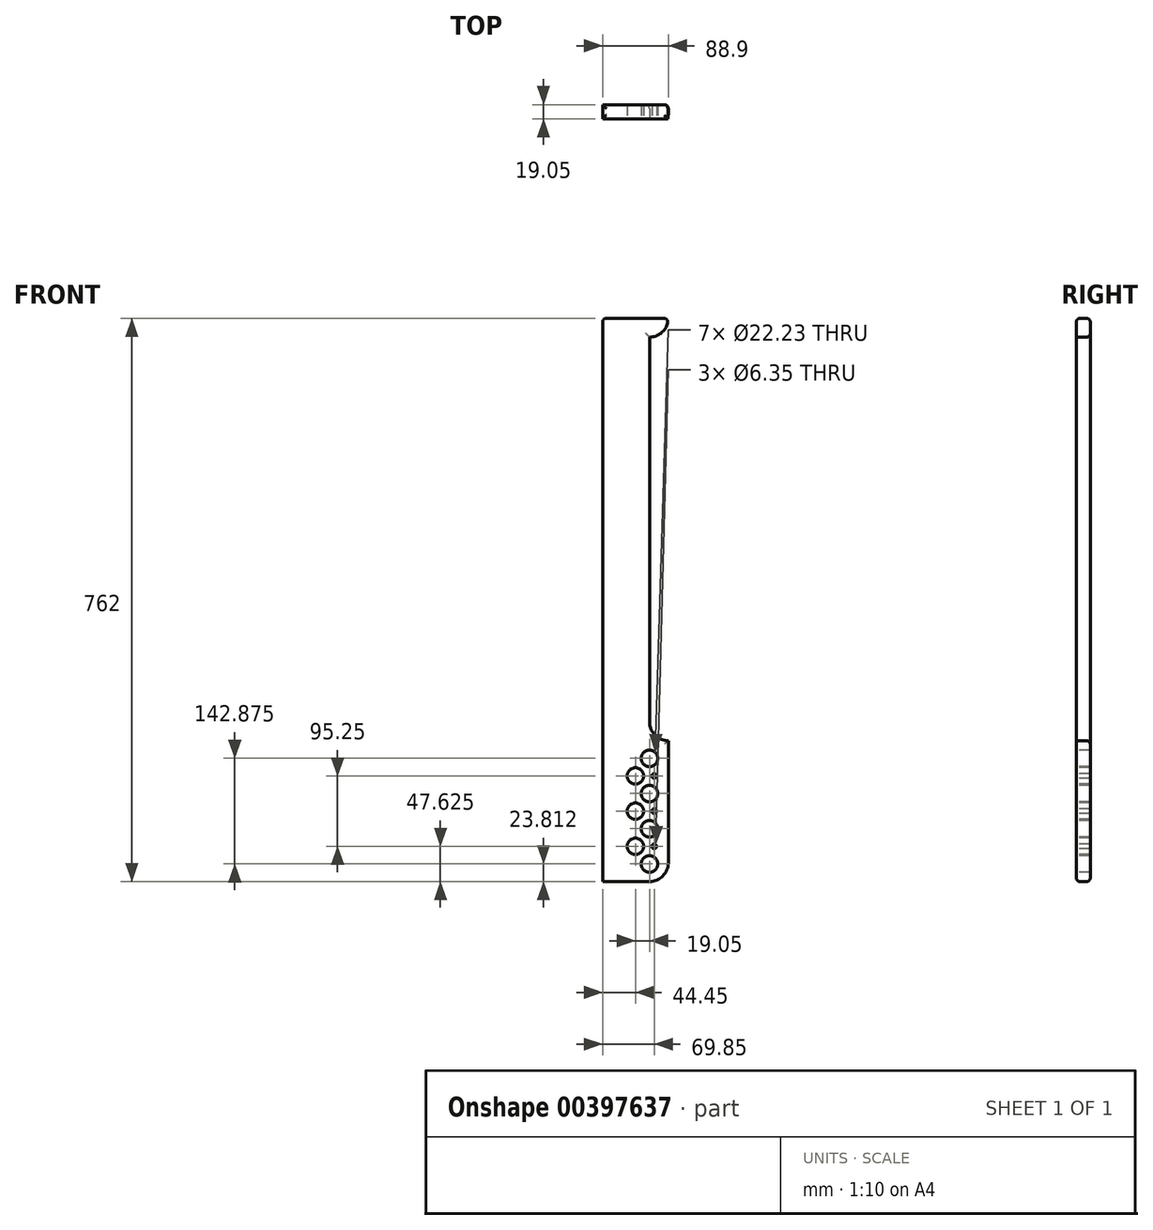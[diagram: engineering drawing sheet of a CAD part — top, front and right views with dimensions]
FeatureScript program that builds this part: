
annotation { "Feature Type Name" : "Feature", "Feature Type Description" : "" }
export const myFeature = defineFeature(function(context is Context, id is Id, definition is map)
    precondition{}
    {
        {
            var Q0;
            Q0=qCreatedBy(makeId("Top.planeOp"),FACE);
            var sketch = newSketch(context, id + "F0", { "sketchPlane" : qUnion([Q0])});
            skLineSegment(sketch, "E0.bottom", {"start": v(0, 0) * mm, "end": v(-88.9, 0) * mm});
            skLineSegment(sketch, "E0.top", {"start": v(0, -19.05) * mm, "end": v(-88.9, -19.05) * mm});
            skLineSegment(sketch, "E0.left", {"start": v(0, 0) * mm, "end": v(0, -19.05) * mm});
            skLineSegment(sketch, "E0.right", {"start": v(-88.9, 0) * mm, "end": v(-88.9, -19.05) * mm});
            skSolve(sketch);
        }
        {
            var Q0;
            Q0 = qSketchRegion(id + "F0", true);
            extrude(context, id + "F1", {"entities" : qUnion([Q0]), "depth" : 762 * mm});
        }
        {
            var Q0;
            Q0=makeQuery(id+"F1.opExtrude","SWEPT_FACE",FACE,{"disambiguationData":[OSD([sQuery(id+"F0.wireOp",EDGE,"E0.right")])]});
            cPlane(context, id + "F2", {"entities" : qUnion([Q0]), "cplaneType" : CPlaneType.OFFSET, "offset" : 44.45 * mm, "oppositeDirection" : true, "width" : 152.4 * mm, "height" : 152.4 * mm});
        }
        {
            var Q0;
            Q0=makeQuery(id+"F1.opExtrude","SWEPT_FACE",FACE,{"disambiguationData":[OSD([sQuery(id+"F0.wireOp",EDGE,"E0.top")])]});
            var sketch = newSketch(context, id + "F3", { "sketchPlane" : qUnion([Q0])});
            skLineSegment(sketch, "E1", {"start": v(0, 762) * mm, "end": v(-25.4, 762) * mm, "construction": true});
            skLineSegment(sketch, "E2", {"start": v(0, 762) * mm, "end": v(0, 762) * mm});
            skLineSegment(sketch, "E3", {"start": v(-25.4, 736.6) * mm, "end": v(-25.4, 736.6) * mm});
            skLineSegment(sketch, "E4", {"start": v(0, 0) * mm, "end": v(0, 190.5) * mm, "construction": true});
            skLineSegment(sketch, "E5", {"start": v(0, 190.5) * mm, "end": v(0, 190.5) * mm});
            skLineSegment(sketch, "E6", {"start": v(-25.4, 215.9) * mm, "end": v(-25.4, 215.9) * mm});
            skLineSegment(sketch, "E7", {"start": v(-25.4, 215.9) * mm, "end": v(-25.4, 736.6) * mm});
            skLineSegment(sketch, "E8", {"start": v(0, 762) * mm, "end": v(104.75, 762) * mm});
            skLineSegment(sketch, "E9", {"start": v(104.75, 762) * mm, "end": v(104.75, 190.5) * mm});
            skLineSegment(sketch, "E10", {"start": v(104.75, 190.5) * mm, "end": v(0, 190.5) * mm});
            skPoint(sketch, "E11.visualSharp", {"position": v(0, 736.6) * mm});
            skArc(sketch, "E11.filletArc", {"start": v(-25.4, 736.6) * mm, "mid": v(-7.44, 744.04) * mm, "end": v(0, 762) * mm});
            skPoint(sketch, "E12.visualSharp", {"position": v(-25.4, 190.5) * mm});
            skArc(sketch, "E12.filletArc", {"start": v(-25.4, 215.9) * mm, "mid": v(-17.96, 197.94) * mm, "end": v(0, 190.5) * mm});
            skSolve(sketch);
        }
        {
            var Q0;
            Q0=makeQuery(id+"F1.opExtrude","SWEPT_FACE",FACE,{"disambiguationData":[OSD([sQuery(id+"F0.wireOp",EDGE,"E0.top")])]});
            var sketch = newSketch(context, id + "F4", { "sketchPlane" : qUnion([Q0])});
            skLineSegment(sketch, "E13", {"start": v(-25.4, 0) * mm, "end": v(-25.4, 0) * mm});
            skLineSegment(sketch, "E14", {"start": v(-25.4, 0) * mm, "end": v(-25.4, 25.4) * mm, "construction": true});
            skLineSegment(sketch, "E15", {"start": v(-25.4, 25.4) * mm, "end": v(0, 25.4) * mm, "construction": true});
            skLineSegment(sketch, "E16", {"start": v(0, 25.4) * mm, "end": v(0, 25.4) * mm});
            skPoint(sketch, "E17.visualSharp", {"position": v(0, 0) * mm});
            skArc(sketch, "E17.filletArc", {"start": v(-25.4, 0) * mm, "mid": v(-7.44, 7.44) * mm, "end": v(0, 25.4) * mm});
            skLineSegment(sketch, "E18", {"start": v(0, 25.4) * mm, "end": v(15.67, 25.4) * mm});
            skLineSegment(sketch, "E19", {"start": v(15.67, 25.4) * mm, "end": v(15.67, -5.8) * mm});
            skLineSegment(sketch, "E20", {"start": v(15.67, -5.8) * mm, "end": v(-25.1, -5.8) * mm});
            skLineSegment(sketch, "E21", {"start": v(-25.1, -5.8) * mm, "end": v(-25.4, 0) * mm});
            skSolve(sketch);
        }
        {
            var Q0;
            Q0 = qSketchRegion(id + "F3", true);
            var Q1;
            Q1 = qSketchRegion(id + "F4", true);
            extrude(context, id + "F5", {"entities" : qUnion([Q0, Q1]), "operationType" : NewBodyOperationType.REMOVE, "oppositeDirection" : true, "depth" : 25.4 * mm});
        }
        {
            var Q0;
            Q0=makeQuery(id+"F1.opExtrude","SWEPT_FACE",FACE,{"disambiguationData":[OSD([sQuery(id+"F0.wireOp",EDGE,"E0.top")])]});
            var sketch = newSketch(context, id + "F6", { "sketchPlane" : qUnion([Q0])});
            skLineSegment(sketch, "E22", {"start": v(0, 0) * mm, "end": v(-44.45, 0) * mm, "construction": true});
            skLineSegment(sketch, "E23", {"start": v(0, 190.5) * mm, "end": v(-44.45, 190.5) * mm, "construction": true});
            skLineSegment(sketch, "E24", {"start": v(-44.45, 190.5) * mm, "end": v(-44.45, 142.88) * mm, "construction": true});
            skLineSegment(sketch, "E25", {"start": v(-44.45, 142.88) * mm, "end": v(-44.45, 95.25) * mm, "construction": true});
            skLineSegment(sketch, "E26", {"start": v(-44.45, 95.25) * mm, "end": v(-44.45, 47.62) * mm, "construction": true});
            skLineSegment(sketch, "E27", {"start": v(-44.45, 47.62) * mm, "end": v(-44.45, 0) * mm, "construction": true});
            skCircle(sketch, "E28", {"center": v(-44.45, 142.88) * mm, "radius": 11.11 * mm});
            skLineSegment(sketch, "E29", {"start": v(-25.4, 142.88) * mm, "end": v(-25.4, 166.69) * mm, "construction": true});
            skCircle(sketch, "E30", {"center": v(-25.4, 166.69) * mm, "radius": 11.11 * mm});
            skLineSegment(sketch, "E31", {"start": v(-33.34, 142.88) * mm, "end": v(-19.05, 142.88) * mm});
            skCircle(sketch, "E32", {"center": v(-19.05, 142.88) * mm, "radius": 3.18 * mm});
            skCircle(sketch, "E33.0.1.0", {"center": v(-44.45, 95.25) * mm, "radius": 11.11 * mm});
            skCircle(sketch, "E33.0.2.0", {"center": v(-44.45, 47.62) * mm, "radius": 11.11 * mm});
            skLineSegment(sketch, "E33.direction1", {"start": v(-44.45, 142.88) * mm, "end": v(-19.05, 142.88) * mm, "construction": true});
            skCircle(sketch, "E34.0.1.0", {"center": v(-25.4, 119.06) * mm, "radius": 11.11 * mm});
            skCircle(sketch, "E34.0.2.0", {"center": v(-25.4, 71.44) * mm, "radius": 11.11 * mm});
            skCircle(sketch, "E34.0.3.0", {"center": v(-25.4, 23.81) * mm, "radius": 11.11 * mm});
            skLineSegment(sketch, "E34.direction1", {"start": v(-25.4, 166.69) * mm, "end": v(6.35, 166.69) * mm, "construction": true});
            skLineSegment(sketch, "E34.direction2", {"start": v(-25.4, 166.69) * mm, "end": v(-25.4, 119.06) * mm, "construction": true});
            skCircle(sketch, "E35.0.1.0", {"center": v(-19.05, 95.25) * mm, "radius": 3.18 * mm});
            skCircle(sketch, "E35.0.2.0", {"center": v(-19.05, 47.62) * mm, "radius": 3.18 * mm});
            skLineSegment(sketch, "E35.direction1", {"start": v(-19.05, 142.88) * mm, "end": v(11.11, 142.88) * mm, "construction": true});
            skLineSegment(sketch, "E35.direction2", {"start": v(-19.05, 142.88) * mm, "end": v(-19.05, 95.25) * mm, "construction": true});
            skLineSegment(sketch, "E36", {"start": v(-44.45, 142.88) * mm, "end": v(-19.05, 142.88) * mm});
            skSolve(sketch);
        }
        {
            var Q0;
            Q0 = qSketchRegion(id + "F6", true);
            extrude(context, id + "F7", {"entities" : qUnion([Q0]), "operationType" : NewBodyOperationType.REMOVE, "oppositeDirection" : true, "depth" : 25.4 * mm});
        }
        {
            var Q0;
            Q0=makeQuery(id+"FR74C55Pt3mRpPs_1.1.F5.boolean.opBoolean","COPY",EDGE,{"derivedFrom":makeQuery(id+"FR74C55Pt3mRpPs_1.1.F5.opExtrude","CAP_EDGE",EDGE,{"disambiguationData":[OSD([sQuery(id+"F3.wireOp",EDGE,"E7")])],"isStart":true})});
            var Q1;
            Q1=makeQuery(id+"FR74C55Pt3mRpPs_1.1.F5.boolean.opBoolean","INTERSECT",EDGE,{"derivedFrom":[makeQuery(id+"F1.opExtrude","SWEPT_FACE",FACE,{"disambiguationData":[OSD([sQuery(id+"F0.wireOp",EDGE,"E0.bottom")])]}),makeQuery(id+"FR74C55Pt3mRpPs_1.1.F5.opExtrude","SWEPT_FACE",FACE,{"disambiguationData":[OSD([sQuery(id+"F3.wireOp",EDGE,"E7")])]})]});
            var Q2;
            Q2=makeQuery(id+"F5.boolean.opBoolean","COPY",EDGE,{"derivedFrom":makeQuery(id+"F5.opExtrude","CAP_EDGE",EDGE,{"disambiguationData":[OSD([sQuery(id+"F3.wireOp",EDGE,"E7")])],"isStart":true})});
            var Q3;
            Q3=makeQuery(id+"F5.boolean.opBoolean","INTERSECT",EDGE,{"derivedFrom":[makeQuery(id+"F1.opExtrude","SWEPT_FACE",FACE,{"disambiguationData":[OSD([sQuery(id+"F0.wireOp",EDGE,"E0.bottom")])]}),makeQuery(id+"F5.opExtrude","SWEPT_FACE",FACE,{"disambiguationData":[OSD([sQuery(id+"F3.wireOp",EDGE,"E7")])]})]});
            var Q4;
            Q4=makeQuery(id+"F1.opExtrude","SWEPT_EDGE",EDGE,{"disambiguationData":[OSD([sQuery(id+"F0.wireOp",EDGE,"E0.top"),sQuery(id+"F0.wireOp",EDGE,"E0.left")])]});
            var Q5;
            Q5=makeQuery(id+"F1.opExtrude","SWEPT_EDGE",EDGE,{"disambiguationData":[OSD([sQuery(id+"F0.wireOp",EDGE,"E0.bottom"),sQuery(id+"F0.wireOp",EDGE,"E0.left")])]});
            var Q6;
            Q6=makeQuery(id+"FR74C55Pt3mRpPs_1.1.F5.boolean.opBoolean","COPY",EDGE,{"derivedFrom":makeQuery(id+"FR74C55Pt3mRpPs_1.1.F5.opExtrude","CAP_EDGE",EDGE,{"disambiguationData":[OSD([sQuery(id+"F3.wireOp",EDGE,"E11.filletArc")])],"isStart":true})});
            var Q7;
            Q7=makeQuery(id+"F1.opExtrude","CAP_EDGE",EDGE,{"disambiguationData":[OSD([sQuery(id+"F0.wireOp",EDGE,"E0.top")])],"isStart":false});
            var Q8;
            Q8=makeQuery(id+"F5.boolean.opBoolean","COPY",EDGE,{"derivedFrom":makeQuery(id+"F5.opExtrude","CAP_EDGE",EDGE,{"disambiguationData":[OSD([sQuery(id+"F3.wireOp",EDGE,"E11.filletArc")])],"isStart":true})});
            var Q9;
            Q9=makeQuery(id+"F5.boolean.opBoolean","INTERSECT",EDGE,{"derivedFrom":[makeQuery(id+"F1.opExtrude","SWEPT_FACE",FACE,{"disambiguationData":[OSD([sQuery(id+"F0.wireOp",EDGE,"E0.bottom")])]}),makeQuery(id+"F5.opExtrude","SWEPT_FACE",FACE,{"disambiguationData":[OSD([sQuery(id+"F3.wireOp",EDGE,"E11.filletArc")])]})]});
            var Q10;
            Q10=makeQuery(id+"F1.opExtrude","CAP_EDGE",EDGE,{"disambiguationData":[OSD([sQuery(id+"F0.wireOp",EDGE,"E0.bottom")])],"isStart":false});
            var Q11;
            Q11=makeQuery(id+"FR74C55Pt3mRpPs_1.1.F5.boolean.opBoolean","INTERSECT",EDGE,{"derivedFrom":[makeQuery(id+"F1.opExtrude","SWEPT_FACE",FACE,{"disambiguationData":[OSD([sQuery(id+"F0.wireOp",EDGE,"E0.bottom")])]}),makeQuery(id+"FR74C55Pt3mRpPs_1.1.F5.opExtrude","SWEPT_FACE",FACE,{"disambiguationData":[OSD([sQuery(id+"F3.wireOp",EDGE,"E11.filletArc")])]})]});
            var Q12;
            Q12=makeQuery(id+"FR74C55Pt3mRpPs_1.1.F5.boolean.opBoolean","COPY",EDGE,{"derivedFrom":makeQuery(id+"FR74C55Pt3mRpPs_1.1.F5.opExtrude","SWEPT_EDGE",EDGE,{"disambiguationData":[OSD([sQuery(id+"F0.wireOp",EDGE,"E0.top"),sQuery(id+"F0.wireOp",EDGE,"E0.left"),sQuery(id+"F3.wireOp",EDGE,"E10"),sQuery(id+"F3.wireOp",EDGE,"E12.filletArc")])]})});
            var Q13;
            Q13=makeQuery(id+"F5.boolean.opBoolean","COPY",EDGE,{"derivedFrom":makeQuery(id+"F5.opExtrude","SWEPT_EDGE",EDGE,{"disambiguationData":[OSD([sQuery(id+"F0.wireOp",EDGE,"E0.top"),sQuery(id+"F0.wireOp",EDGE,"E0.left"),sQuery(id+"F3.wireOp",EDGE,"E10"),sQuery(id+"F3.wireOp",EDGE,"E12.filletArc")])]})});
            var Q14;
            {var subQ0=sQuery(id+"F0.wireOp",EDGE,"E0.left");Q14=makeQuery(id+"F5.boolean.opBoolean","MERGE",EDGE,{"derivedFrom":[makeQuery(id+"F1.opExtrude","CAP_EDGE",EDGE,{"disambiguationData":[OSD([subQ0])],"isStart":false}),makeQuery(id+"F5.opExtrude","SWEPT_EDGE",EDGE,{"disambiguationData":[OSD([sQuery(id+"F0.wireOp",EDGE,"E0.top"),subQ0,sQuery(id+"F3.wireOp",EDGE,"E8"),sQuery(id+"F3.wireOp",EDGE,"E11.filletArc")])]})]});}
            var Q15;
            Q15=makeQuery(id+"FR74C55Pt3mRpPs_1.1.F5.boolean.opBoolean","MERGE",EDGE,{"derivedFrom":[makeQuery(id+"F1.opExtrude","CAP_EDGE",EDGE,{"disambiguationData":[OSD([sQuery(id+"F0.wireOp",EDGE,"E0.right")])],"isStart":false}),makeQuery(id+"FR74C55Pt3mRpPs_1.1.F5.opExtrude","SWEPT_EDGE",EDGE,{"disambiguationData":[OSD([sQuery(id+"F0.wireOp",EDGE,"E0.top"),sQuery(id+"F0.wireOp",EDGE,"E0.left"),sQuery(id+"F3.wireOp",EDGE,"E8"),sQuery(id+"F3.wireOp",EDGE,"E11.filletArc")])]})]});
            fillet(context, id + "F8", {"entities" : qUnion([Q0, Q1, Q2, Q3, Q4, Q5, Q6, Q7, Q8, Q9, Q10, Q11, Q12, Q13, Q14, Q15]), "radius" : 5.08 * mm, "tangentPropagation" : true, "allowEdgeOverflow" : false});
        }
    });
